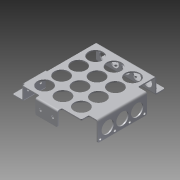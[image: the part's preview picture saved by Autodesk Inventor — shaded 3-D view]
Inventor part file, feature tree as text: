
AUTODESK INVENTOR PART (.ipt)
format: ipt  version: 2014 SP1 (Build 180222100, 222)  size: 633,856 bytes
history: native  units: in
note: dims shown in document units (in); Inventor stores cm internally (conversion verified against a paired STEP export)
features: sheet_metal_op x15, other x15, sketch x13, chamfer x2, reference x2
ambient origin geometry x8: Origin, YZ Plane, XZ Plane, XY Plane, X Axis, Y Axis, Z Axis, Center Point
bodies: Solid1 (feature_tree)
feature tree (47):
  sheet_metal_op  "Face1"
  sheet_metal_op  "Flange1"
  sheet_metal_op  "Flange2"
  sketch  "Sketch4"  dims[d3=0.5in]
  sheet_metal_op  "Face2"
  sheet_metal_op  "Flange3"
  sheet_metal_op  "Flange4"
  chamfer  "Corner Round1"
  sheet_metal_op  "Flange5"
  sheet_metal_op  "Flange6"
  chamfer  "Corner Round2"
  sketch  "Sketch1"  dims[d0=1.0in]
  other  "Plate1"
  sketch  "Sketch2"  dims[d1=6.0in]
  other  "Plate2"
  sheet_metal_op  "Bend1"
  sketch  "Sketch3"  dims[d2=0.26in]
  other  "Plate3"
  sheet_metal_op  "Bend2"
  other  "Plate4"
  sheet_metal_op  "Bend3"
  sketch  "Sketch5"  dims[d4=2.3622in d6=1.0in d7=0.3937in d9=1.0in]
  other  "Plate5"
  sheet_metal_op  "Bend4"
  sketch  "Sketch6"  dims[d11=0.5in]
  other  "Plate6"
  sheet_metal_op  "Bend5"
  sketch  "Sketch7"  dims[d12=0.125in]
  sketch  "Sketch8"  dims[d13=0.125in]
  sketch  "Sketch9"  dims[d14=0.0625in]
  other  "Plate7"
  sheet_metal_op  "Bend6"
  sketch  "Sketch10"  dims[d15=0.25in]
  other  "Plate8"
  sheet_metal_op  "Bend7"
  reference  "Reference10"
  reference  "Reference11"
  sketch  "Sketch11"  dims[d16=0.125in]
  sketch  "Sketch12"  dims[d17=1.5in d18=90.0deg d19=0.05in]
  sketch  "Sketch13"  dims[d20=0.5in d21=0.125in d22=0.125in d23=0.125in d24=0.0625in d25=0.25in d26=0.125in d27=7.625in d28=90.0deg d29=0.05in d30=0.5in d31=0.125in d32=0.125in d33=2.25in d35=0.25in d36=0.125in d37=0.125in d38=0.0625in d39=0.25in d40=0.125in d41=0.125in d42=0.0625in d43=0.25in d44=0.125in d45=1.625in d46=90.0deg d47=0.05in d48=0.5in d49=0.125in d50=0.125in d51=0.125in d52=0.0625in d53=0.25in d54=0.125in d55=1.125in d56=90.0deg d57=0.05in d58=0.5in d59=0.125in d60=0.125in d61=0.125in d62=0.0in d63=0.125in d64=1.5in d65=1.125in d66=1.125in d67=1.5748in d69=1.7333in d70=1.1811in d72=1.875in d75=1.125in d76=1.125in d77=0.125in d78=0.0in d79=0.875in d83=0.75in d84=6.0in d85=1.9685in d87=1.125in d88=0.3937in d90=1.0in d92=0.125in d93=0.0in d95=5.0in d96=0.125in d97=0.0625in d98=0.25in d99=0.125in d100=2.0in d101=90.0deg d102=0.05in d103=0.5in d104=0.125in d105=0.125in d106=0.25in d107=2.25in d108=2.0in d109=0.125in d110=0.0625in d111=0.25in d112=0.125in d113=1.5in d114=90.0deg d115=0.05in d116=0.5in d117=0.125in d118=0.125in d119=0.75in d120=0.75in d121=0.25in d122=5.0in d123=1.25in d124=1.0in d125=1.1811in d127=1.5in d128=0.3937in d130=1.0in d132=1.0in d133=0.25in d134=0.26in d135=0.25in d136=1.5748in d138=1.5in d139=0.3937in d141=1.0in d143=0.25in d144=0.125in d145=0.0in d146=7.45in d147=0.26in d149=0.5in d150=0.5in d151=0.125in d152=0.0in d153=0.26in d155=0.5in d156=0.5in d157=0.125in d158=0.0in d159=0.125in d5=0.0312in d8=0.0625in d10=0.0312in]
  other  "Cut1"
  other  "Cut2"
  other  "Cut3"
  other  "Cut4"
  other  "Cut5"
  other  "Cut6"
  other  "Definition1"
